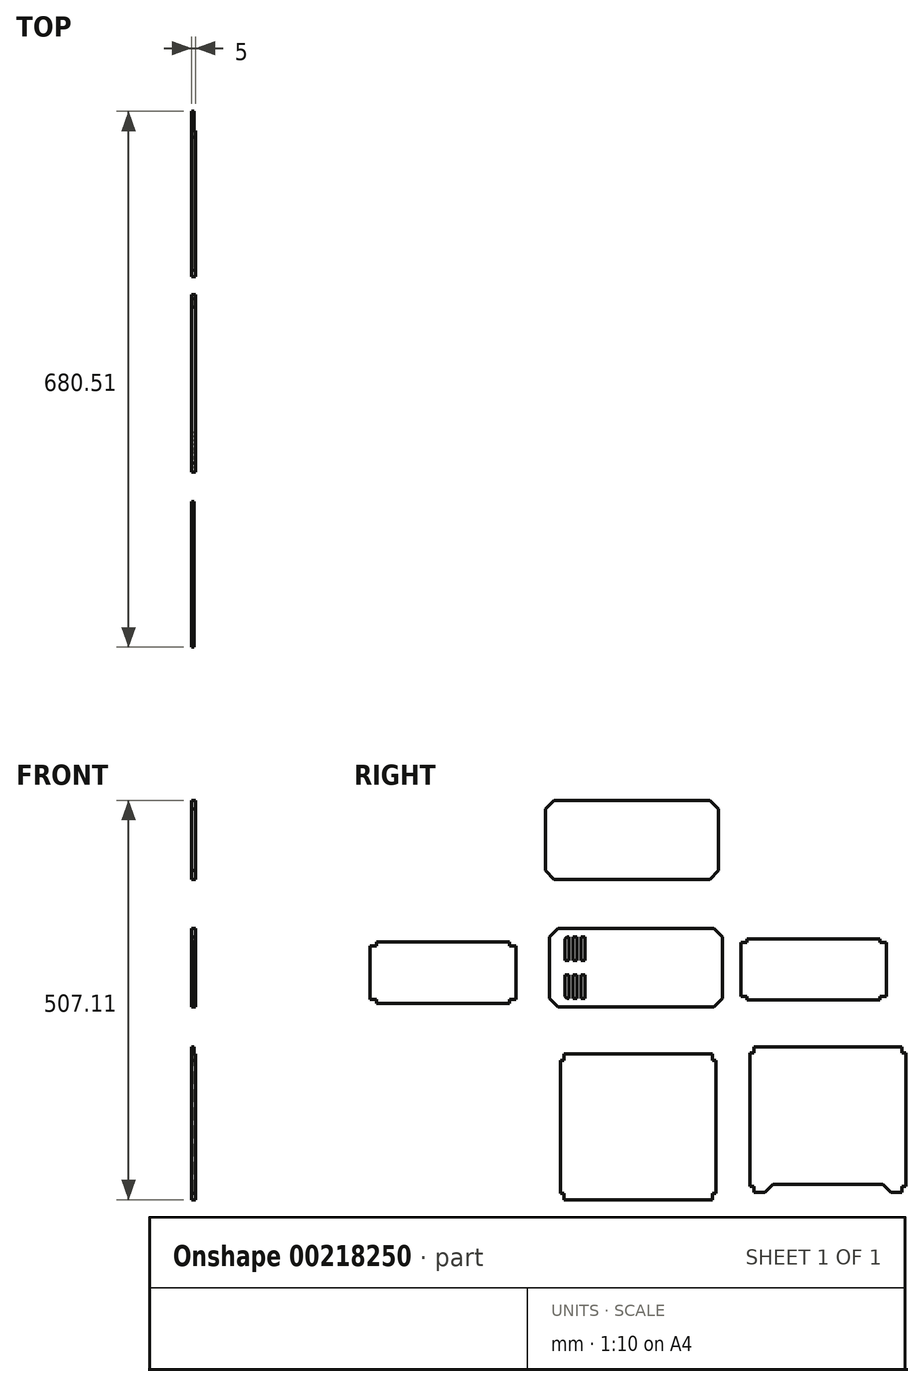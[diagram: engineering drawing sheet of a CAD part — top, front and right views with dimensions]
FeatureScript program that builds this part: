
annotation { "Feature Type Name" : "Feature", "Feature Type Description" : "" }
export const myFeature = defineFeature(function(context is Context, id is Id, definition is map)
    precondition{}
    {
        {
            var Q0;
            Q0=qCreatedBy(makeId("Right.planeOp"),FACE);
            var sketch = newSketch(context, id + "F0", { "sketchPlane" : qUnion([Q0])});
            skLineSegment(sketch, "E0.bottom", {"start": v(118.5, 69) * mm, "end": v(-101.5, 69) * mm});
            skLineSegment(sketch, "E0.top", {"start": v(118.5, -31) * mm, "end": v(-101.5, -31) * mm});
            skLineSegment(sketch, "E0.left", {"start": v(118.5, 69) * mm, "end": v(118.5, -31) * mm});
            skLineSegment(sketch, "E0.right", {"start": v(-101.5, 69) * mm, "end": v(-101.5, -31) * mm});
            skLineSegment(sketch, "E1", {"start": v(-101.5, -20) * mm, "end": v(-90.5, -31) * mm});
            skLineSegment(sketch, "E2", {"start": v(-101.5, 58) * mm, "end": v(-90.5, 69) * mm});
            skLineSegment(sketch, "E3", {"start": v(107.5, 69) * mm, "end": v(118.5, 58) * mm});
            skLineSegment(sketch, "E4", {"start": v(107.5, -31) * mm, "end": v(118.5, -20) * mm});
            skSolve(sketch);
        }
        {
            var Q0;
            {var subQ0=sQuery(id+"F0.wireOp",EDGE,"E1");Q0=makeQuery(id+"F0.imprint","IMPRINT",FACE,{"disambiguationData":[TD([[makeQuery(id+"F0.imprint","IMPRINT",EDGE,{"derivedFrom":subQ0}),1.0]])]});}
            extrude(context, id + "F1", {"entities" : qUnion([Q0]), "depth" : 5 * mm});
        }
        {
            var Q0;
            Q0=qCreatedBy(makeId("Right.planeOp"),FACE);
            var sketch = newSketch(context, id + "F2", { "sketchPlane" : qUnion([Q0])});
            skLineSegment(sketch, "E5.bottom", {"start": v(-329.25, 51.55) * mm, "end": v(-144.25, 51.55) * mm});
            skLineSegment(sketch, "E5.top", {"start": v(-329.25, -26.45) * mm, "end": v(-144.25, -26.45) * mm});
            skLineSegment(sketch, "E5.left", {"start": v(-329.25, 51.55) * mm, "end": v(-329.25, -26.45) * mm});
            skLineSegment(sketch, "E5.right", {"start": v(-144.25, 51.55) * mm, "end": v(-144.25, -26.45) * mm});
            skLineSegment(sketch, "E6", {"start": v(-144.25, -21.45) * mm, "end": v(-152.25, -21.45) * mm});
            skLineSegment(sketch, "E7", {"start": v(-152.25, -21.45) * mm, "end": v(-152.25, -26.45) * mm});
            skLineSegment(sketch, "E8", {"start": v(-144.25, 46.55) * mm, "end": v(-152.25, 46.55) * mm});
            skLineSegment(sketch, "E9", {"start": v(-152.25, 46.55) * mm, "end": v(-152.25, 51.55) * mm});
            skLineSegment(sketch, "E10", {"start": v(-321.25, 51.55) * mm, "end": v(-321.25, 46.55) * mm});
            skLineSegment(sketch, "E11", {"start": v(-321.25, 46.55) * mm, "end": v(-329.25, 46.55) * mm});
            skLineSegment(sketch, "E12", {"start": v(-329.25, -21.45) * mm, "end": v(-321.25, -21.45) * mm});
            skLineSegment(sketch, "E13", {"start": v(-321.25, -21.45) * mm, "end": v(-321.25, -26.45) * mm});
            skSolve(sketch);
        }
        {
            var Q0;
            {var subQ3=sQuery(id+"F2.wireOp",EDGE,"E6");Q0=makeQuery(id+"F2.imprint","IMPRINT",FACE,{"disambiguationData":[TD([[makeQuery(id+"F2.imprint","IMPRINT",EDGE,{"derivedFrom":subQ3}),-1.0]])]});}
            extrude(context, id + "F3", {"entities" : qUnion([Q0]), "depth" : 3 * mm});
        }
        {
            var Q0;
            Q0=qCreatedBy(makeId("Right.planeOp"),FACE);
            var sketch = newSketch(context, id + "F4", { "sketchPlane" : qUnion([Q0])});
            skLineSegment(sketch, "E14.bottom", {"start": v(113.2, 231.33) * mm, "end": v(-106.8, 231.33) * mm});
            skLineSegment(sketch, "E14.top", {"start": v(113.2, 131.33) * mm, "end": v(-106.8, 131.33) * mm});
            skLineSegment(sketch, "E14.left", {"start": v(113.2, 231.33) * mm, "end": v(113.2, 131.33) * mm});
            skLineSegment(sketch, "E14.right", {"start": v(-106.8, 231.33) * mm, "end": v(-106.8, 131.33) * mm});
            skLineSegment(sketch, "E15", {"start": v(-106.8, 142.33) * mm, "end": v(-95.8, 131.33) * mm});
            skLineSegment(sketch, "E16", {"start": v(-106.8, 220.33) * mm, "end": v(-95.8, 231.33) * mm});
            skLineSegment(sketch, "E17", {"start": v(102.2, 231.33) * mm, "end": v(113.2, 220.33) * mm});
            skLineSegment(sketch, "E18", {"start": v(102.2, 131.33) * mm, "end": v(113.2, 142.33) * mm});
            skSolve(sketch);
        }
        {
            var Q0;
            {var subQ0=sQuery(id+"F4.wireOp",EDGE,"E15");Q0=makeQuery(id+"F4.imprint","IMPRINT",FACE,{"disambiguationData":[TD([[makeQuery(id+"F4.imprint","IMPRINT",EDGE,{"derivedFrom":subQ0}),1.0]])]});}
            extrude(context, id + "F5", {"entities" : qUnion([Q0]), "depth" : 5 * mm});
        }
        {
            var Q0;
            Q0=qCreatedBy(makeId("Right.planeOp"),FACE);
            var sketch = newSketch(context, id + "F6", { "sketchPlane" : qUnion([Q0])});
            skLineSegment(sketch, "E19.bottom", {"start": v(141.52, 55.7) * mm, "end": v(326.52, 55.7) * mm});
            skLineSegment(sketch, "E19.top", {"start": v(141.52, -22.3) * mm, "end": v(326.52, -22.3) * mm});
            skLineSegment(sketch, "E19.left", {"start": v(141.52, 55.7) * mm, "end": v(141.52, -22.3) * mm});
            skLineSegment(sketch, "E19.right", {"start": v(326.52, 55.7) * mm, "end": v(326.52, -22.3) * mm});
            skLineSegment(sketch, "E20", {"start": v(326.52, -17.3) * mm, "end": v(318.52, -17.3) * mm});
            skLineSegment(sketch, "E21", {"start": v(318.52, -17.3) * mm, "end": v(318.52, -22.3) * mm});
            skLineSegment(sketch, "E22", {"start": v(326.52, 50.7) * mm, "end": v(318.52, 50.7) * mm});
            skLineSegment(sketch, "E23", {"start": v(318.52, 50.7) * mm, "end": v(318.52, 55.7) * mm});
            skLineSegment(sketch, "E24", {"start": v(149.52, 55.7) * mm, "end": v(149.52, 50.7) * mm});
            skLineSegment(sketch, "E25", {"start": v(149.52, 50.7) * mm, "end": v(141.52, 50.7) * mm});
            skLineSegment(sketch, "E26", {"start": v(141.52, -17.3) * mm, "end": v(149.52, -17.3) * mm});
            skLineSegment(sketch, "E27", {"start": v(149.52, -17.3) * mm, "end": v(149.52, -22.3) * mm});
            skSolve(sketch);
        }
        {
            var Q0;
            {var subQ5=sQuery(id+"F6.wireOp",EDGE,"E20");Q0=makeQuery(id+"F6.imprint","IMPRINT",FACE,{"disambiguationData":[TD([[makeQuery(id+"F6.imprint","IMPRINT",EDGE,{"derivedFrom":subQ5}),-1.0]])]});}
            extrude(context, id + "F7", {"entities" : qUnion([Q0]), "depth" : 5 * mm});
        }
        {
            var Q0;
            Q0=qCreatedBy(makeId("Right.planeOp"),FACE);
            var sketch = newSketch(context, id + "F8", { "sketchPlane" : qUnion([Q0])});
            skLineSegment(sketch, "E28.bottom", {"start": v(110.28, -90.78) * mm, "end": v(110.28, -275.78) * mm});
            skLineSegment(sketch, "E28.top", {"start": v(-87.72, -90.78) * mm, "end": v(-87.72, -275.78) * mm});
            skLineSegment(sketch, "E28.left", {"start": v(110.28, -90.78) * mm, "end": v(-87.72, -90.78) * mm});
            skLineSegment(sketch, "E28.right", {"start": v(110.28, -275.78) * mm, "end": v(-87.72, -275.78) * mm});
            skLineSegment(sketch, "E29", {"start": v(-82.72, -275.78) * mm, "end": v(-82.72, -267.78) * mm});
            skLineSegment(sketch, "E30", {"start": v(-82.72, -267.78) * mm, "end": v(-87.72, -267.78) * mm});
            skLineSegment(sketch, "E31", {"start": v(105.28, -275.78) * mm, "end": v(105.28, -267.78) * mm});
            skLineSegment(sketch, "E32", {"start": v(105.28, -267.78) * mm, "end": v(110.28, -267.78) * mm});
            skLineSegment(sketch, "E33", {"start": v(110.28, -98.78) * mm, "end": v(105.28, -98.78) * mm});
            skLineSegment(sketch, "E34", {"start": v(105.28, -98.78) * mm, "end": v(105.28, -90.78) * mm});
            skLineSegment(sketch, "E35", {"start": v(-82.72, -90.78) * mm, "end": v(-82.72, -98.78) * mm});
            skLineSegment(sketch, "E36", {"start": v(-82.72, -98.78) * mm, "end": v(-87.72, -98.78) * mm});
            skSolve(sketch);
        }
        {
            var Q0;
            {var subQ3=sQuery(id+"F8.wireOp",EDGE,"E29");Q0=makeQuery(id+"F8.imprint","IMPRINT",FACE,{"disambiguationData":[TD([[makeQuery(id+"F8.imprint","IMPRINT",EDGE,{"derivedFrom":subQ3}),-1.0]])]});}
            extrude(context, id + "F9", {"entities" : qUnion([Q0]), "depth" : 5 * mm});
        }
        {
            var Q0;
            Q0=qCreatedBy(makeId("Right.planeOp"),FACE);
            var sketch = newSketch(context, id + "F10", { "sketchPlane" : qUnion([Q0])});
            skLineSegment(sketch, "E37.bottom", {"start": v(351.26, -81.6) * mm, "end": v(351.26, -266.6) * mm});
            skLineSegment(sketch, "E37.top", {"start": v(153.26, -81.6) * mm, "end": v(153.26, -266.6) * mm});
            skLineSegment(sketch, "E37.left", {"start": v(351.26, -81.6) * mm, "end": v(153.26, -81.6) * mm});
            skLineSegment(sketch, "E37.right", {"start": v(351.26, -266.6) * mm, "end": v(153.26, -266.6) * mm});
            skLineSegment(sketch, "E38", {"start": v(158.26, -266.6) * mm, "end": v(158.26, -258.6) * mm});
            skLineSegment(sketch, "E39", {"start": v(158.26, -258.6) * mm, "end": v(153.26, -258.6) * mm});
            skLineSegment(sketch, "E40", {"start": v(346.26, -266.6) * mm, "end": v(346.26, -258.6) * mm});
            skLineSegment(sketch, "E41", {"start": v(346.26, -258.6) * mm, "end": v(351.26, -258.6) * mm});
            skLineSegment(sketch, "E42", {"start": v(351.26, -89.6) * mm, "end": v(346.26, -89.6) * mm});
            skLineSegment(sketch, "E43", {"start": v(346.26, -89.6) * mm, "end": v(346.26, -81.6) * mm});
            skLineSegment(sketch, "E44", {"start": v(158.26, -81.6) * mm, "end": v(158.26, -89.6) * mm});
            skLineSegment(sketch, "E45", {"start": v(158.26, -89.6) * mm, "end": v(153.26, -89.6) * mm});
            skSolve(sketch);
        }
        {
            var Q0;
            {var subQ1=sQuery(id+"F10.wireOp",EDGE,"E38");Q0=makeQuery(id+"F10.imprint","IMPRINT",FACE,{"disambiguationData":[TD([[makeQuery(id+"F10.imprint","IMPRINT",EDGE,{"derivedFrom":subQ1}),-1.0]])]});}
            extrude(context, id + "F11", {"entities" : qUnion([Q0]), "depth" : 3 * mm});
        }
        {
            var Q0;
            Q0=makeQuery(id+"F11.opExtrude","CAP_FACE",FACE,{"disambiguationData":[OSD([sQuery(id+"F10.wireOp",EDGE,"E37.bottom"),sQuery(id+"F10.wireOp",EDGE,"E37.top"),sQuery(id+"F10.wireOp",EDGE,"E37.left"),sQuery(id+"F10.wireOp",EDGE,"E37.right"),sQuery(id+"F10.wireOp",EDGE,"E38"),sQuery(id+"F10.wireOp",EDGE,"E39"),sQuery(id+"F10.wireOp",EDGE,"E40"),sQuery(id+"F10.wireOp",EDGE,"E41"),sQuery(id+"F10.wireOp",EDGE,"E42"),sQuery(id+"F10.wireOp",EDGE,"E43"),sQuery(id+"F10.wireOp",EDGE,"E44"),sQuery(id+"F10.wireOp",EDGE,"E45")])],"isStart":false});
            var sketch = newSketch(context, id + "F12", { "sketchPlane" : qUnion([Q0])});
            skLineSegment(sketch, "E46", {"start": v(172.26, -266.6) * mm, "end": v(182.26, -256.6) * mm});
            skLineSegment(sketch, "E47", {"start": v(182.26, -256.6) * mm, "end": v(322.26, -256.6) * mm});
            skLineSegment(sketch, "E48", {"start": v(322.26, -256.6) * mm, "end": v(332.26, -266.6) * mm});
            skLineSegment(sketch, "E49", {"start": v(252.26, -256.6) * mm, "end": v(252.26, -266.6) * mm, "construction": true});
            skSolve(sketch);
        }
        {
            var Q0;
            {var subQ0=sQuery(id+"F12.wireOp",EDGE,"E46");Q0=makeQuery(id+"F12.imprint","IMPRINT",FACE,{"disambiguationData":[TD([[makeQuery(id+"F12.imprint","IMPRINT",EDGE,{"derivedFrom":subQ0}),-1.0]])]});}
            extrude(context, id + "F13", {"entities" : qUnion([Q0]), "operationType" : NewBodyOperationType.REMOVE, "oppositeDirection" : true, "depth" : 25 * mm});
        }
        {
            var Q0;
            Q0=makeQuery(id+"F1.opExtrude","CAP_FACE",FACE,{"disambiguationData":[OSD([sQuery(id+"F0.wireOp",EDGE,"E0.bottom"),sQuery(id+"F0.wireOp",EDGE,"E0.top"),sQuery(id+"F0.wireOp",EDGE,"E0.left"),sQuery(id+"F0.wireOp",EDGE,"E0.right"),sQuery(id+"F0.wireOp",EDGE,"E1"),sQuery(id+"F0.wireOp",EDGE,"E2"),sQuery(id+"F0.wireOp",EDGE,"E3"),sQuery(id+"F0.wireOp",EDGE,"E4")])],"isStart":false});
            var sketch = newSketch(context, id + "F14", { "sketchPlane" : qUnion([Q0])});
            skLineSegment(sketch, "E50", {"start": v(-76.5, 69) * mm, "end": v(-76.5, 58) * mm, "construction": true});
            skLineSegment(sketch, "E51.bottom", {"start": v(-76.5, 58) * mm, "end": v(-81.5, 58) * mm});
            skLineSegment(sketch, "E51.top", {"start": v(-76.5, 28) * mm, "end": v(-81.5, 28) * mm});
            skLineSegment(sketch, "E51.left", {"start": v(-76.5, 58) * mm, "end": v(-76.5, 28) * mm});
            skLineSegment(sketch, "E51.right", {"start": v(-81.5, 58) * mm, "end": v(-81.5, 28) * mm});
            skLineSegment(sketch, "E52", {"start": v(-81.5, 58) * mm, "end": v(-101.5, 58) * mm, "construction": true});
            skLineSegment(sketch, "E53", {"start": v(-76.5, 28) * mm, "end": v(-76.5, 10) * mm, "construction": true});
            skLineSegment(sketch, "E54.bottom", {"start": v(-76.5, 10) * mm, "end": v(-81.5, 10) * mm});
            skLineSegment(sketch, "E54.top", {"start": v(-76.5, -20) * mm, "end": v(-81.5, -20) * mm});
            skLineSegment(sketch, "E54.left", {"start": v(-76.5, 10) * mm, "end": v(-76.5, -20) * mm});
            skLineSegment(sketch, "E54.right", {"start": v(-81.5, 10) * mm, "end": v(-81.5, -20) * mm});
            skLineSegment(sketch, "E55", {"start": v(-76.5, -20) * mm, "end": v(-76.5, -31) * mm, "construction": true});
            skLineSegment(sketch, "E56", {"start": v(-76.5, 28) * mm, "end": v(-71.5, 28) * mm, "construction": true});
            skLineSegment(sketch, "E57.bottom", {"start": v(-71.5, 28) * mm, "end": v(-66.5, 28) * mm});
            skLineSegment(sketch, "E57.top", {"start": v(-71.5, 58) * mm, "end": v(-66.5, 58) * mm});
            skLineSegment(sketch, "E57.left", {"start": v(-71.5, 28) * mm, "end": v(-71.5, 58) * mm});
            skLineSegment(sketch, "E57.right", {"start": v(-66.5, 28) * mm, "end": v(-66.5, 58) * mm});
            skLineSegment(sketch, "E58", {"start": v(-76.5, 10) * mm, "end": v(-71.5, 10) * mm, "construction": true});
            skLineSegment(sketch, "E59.bottom", {"start": v(-71.5, 10) * mm, "end": v(-66.5, 10) * mm});
            skLineSegment(sketch, "E59.top", {"start": v(-71.5, -20) * mm, "end": v(-66.5, -20) * mm});
            skLineSegment(sketch, "E59.left", {"start": v(-71.5, 10) * mm, "end": v(-71.5, -20) * mm});
            skLineSegment(sketch, "E59.right", {"start": v(-66.5, 10) * mm, "end": v(-66.5, -20) * mm});
            skLineSegment(sketch, "E60", {"start": v(-66.5, 58) * mm, "end": v(-61.5, 58) * mm, "construction": true});
            skLineSegment(sketch, "E61.bottom", {"start": v(-61.5, 58) * mm, "end": v(-56.5, 58) * mm});
            skLineSegment(sketch, "E61.top", {"start": v(-61.5, 28) * mm, "end": v(-56.5, 28) * mm});
            skLineSegment(sketch, "E61.left", {"start": v(-61.5, 58) * mm, "end": v(-61.5, 28) * mm});
            skLineSegment(sketch, "E61.right", {"start": v(-56.5, 58) * mm, "end": v(-56.5, 28) * mm});
            skLineSegment(sketch, "E62", {"start": v(-66.5, 10) * mm, "end": v(-61.5, 10) * mm, "construction": true});
            skLineSegment(sketch, "E63.bottom", {"start": v(-61.5, 10) * mm, "end": v(-56.5, 10) * mm});
            skLineSegment(sketch, "E63.top", {"start": v(-61.5, -20) * mm, "end": v(-56.5, -20) * mm});
            skLineSegment(sketch, "E63.left", {"start": v(-61.5, 10) * mm, "end": v(-61.5, -20) * mm});
            skLineSegment(sketch, "E63.right", {"start": v(-56.5, 10) * mm, "end": v(-56.5, -20) * mm});
            skSolve(sketch);
        }
        {
            var Q0;
            Q0=qSketchRegion(id+"F14",true);
            extrude(context, id + "F15", {"entities" : qUnion([Q0]), "operationType" : NewBodyOperationType.REMOVE, "oppositeDirection" : true, "depth" : 25 * mm});
        }
        {
            var Q0;
            Q0=makeQuery(id+"F15.boolean.opBoolean","COPY",EDGE,{"derivedFrom":makeQuery(id+"F15.opExtrude","SWEPT_EDGE",EDGE,{"disambiguationData":[OSD([sQuery(id+"F14.wireOp",EDGE,"E54.top"),sQuery(id+"F14.wireOp",EDGE,"E54.right")])]})});
            var Q1;
            Q1=makeQuery(id+"F15.boolean.opBoolean","COPY",EDGE,{"derivedFrom":makeQuery(id+"F15.opExtrude","SWEPT_EDGE",EDGE,{"disambiguationData":[OSD([sQuery(id+"F14.wireOp",EDGE,"E51.bottom"),sQuery(id+"F14.wireOp",EDGE,"E51.right")])]})});
            chamfer(context, id + "F16", {"entities" : qUnion([Q0, Q1]), "width" : 2.5 * mm, "tangentPropagation" : true});
        }
    });
